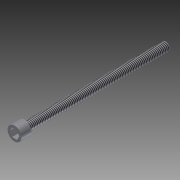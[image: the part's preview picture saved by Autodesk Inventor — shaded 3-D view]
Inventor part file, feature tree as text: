
AUTODESK INVENTOR PART (.ipt)
format: ipt  version: 2012 (Build 160160000, 160)  size: 87,552 bytes
history: native  units: in
note: dims shown in document units (in); Inventor stores cm internally (conversion verified against a paired STEP export)
features: extrude x2, sketch x1, thread x1
ambient origin geometry x8: Origin, YZ Plane, XZ Plane, XY Plane, X Axis, Y Axis, Z Axis, Center Point
bodies: Solid1 (feature_tree)
feature tree (4):
  sketch  "Sketch1"  dims[d0=0.164in d1=0.27in d2=2.75in d3=0.0in d4=0.2in d5=0.0in d6=1.0in d7=0.0in]
  extrude  "Extrusion1"  Depth=0.27in
  extrude  "Extrusion2"  Depth=2.75in TaperAngle=0.0deg
  thread  "Thread1"  [1 undecoded]
note: 1 required parameter value undecoded (feature->parameter linkage not recoverable at this tier; creation-order binding heuristic only, values carry confidence <= 0.55)
